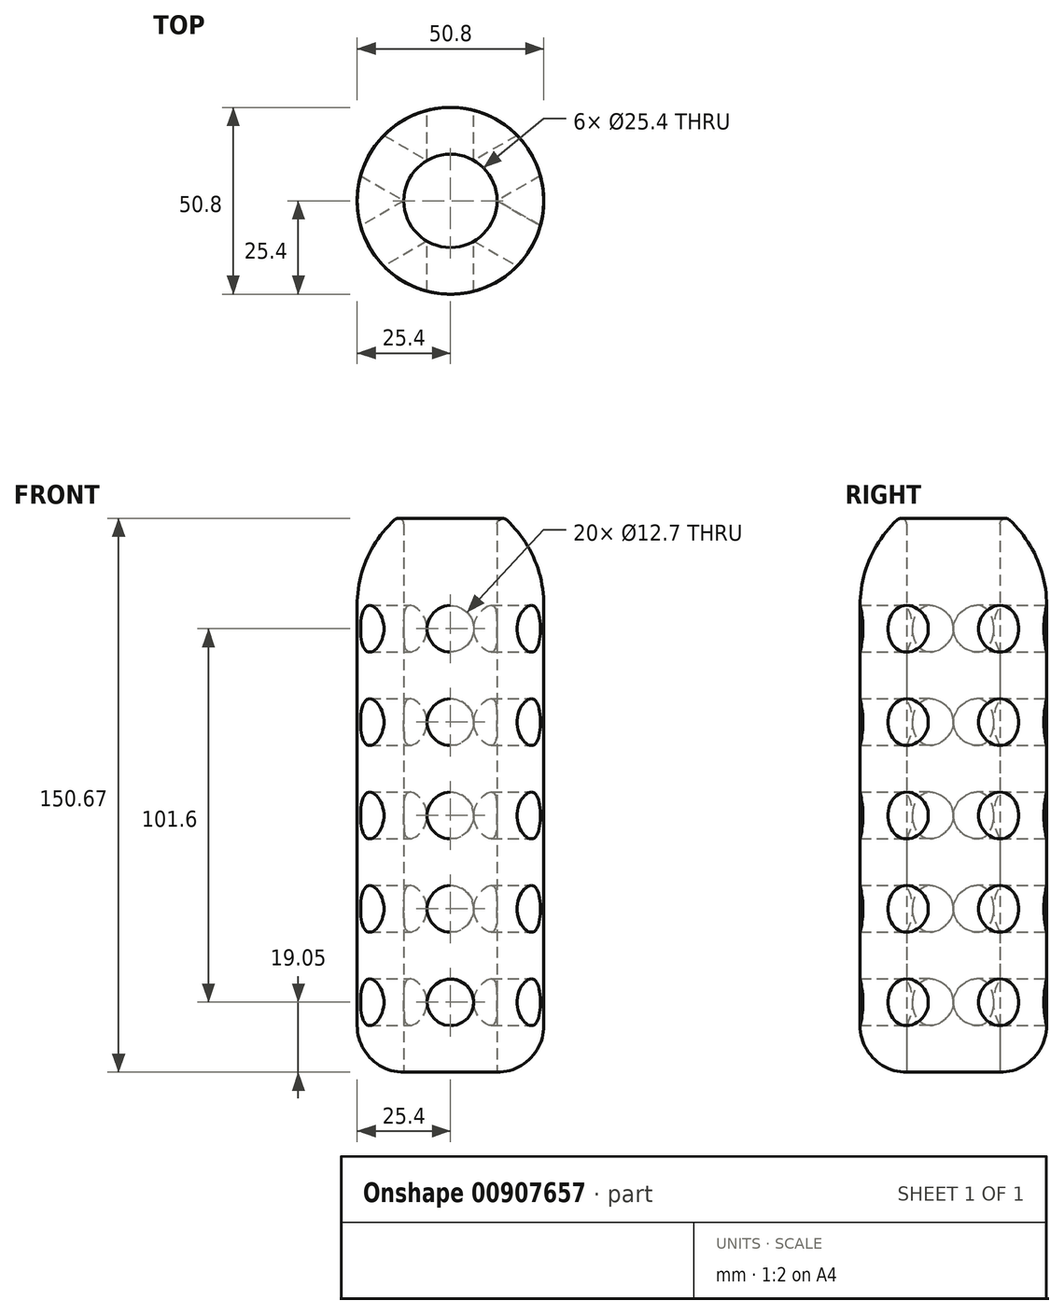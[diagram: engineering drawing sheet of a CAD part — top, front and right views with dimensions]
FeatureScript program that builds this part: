
annotation { "Feature Type Name" : "Feature", "Feature Type Description" : "" }
export const myFeature = defineFeature(function(context is Context, id is Id, definition is map)
    precondition{}
    {
        {
            var Q0;
            Q0=qCreatedBy(makeId("Front.planeOp"),FACE);
            var sketch = newSketch(context, id + "F0", { "sketchPlane" : qUnion([Q0])});
            skLineSegment(sketch, "E0", {"start": v(0, 0) * mm, "end": v(25.4, 0) * mm});
            skLineSegment(sketch, "E1", {"start": v(25.4, 0) * mm, "end": v(25.4, 127) * mm});
            skLineSegment(sketch, "E2", {"start": v(0, 0) * mm, "end": v(0, 152.4) * mm});
            skLineSegment(sketch, "E3", {"start": v(0, 152.4) * mm, "end": v(12.7, 152.4) * mm});
            skArc(sketch, "E4", {"start": v(25.4, 127) * mm, "mid": v(22.05, 141.2) * mm, "end": v(12.7, 152.4) * mm});
            skSolve(sketch);
        }
        {
            var Q0;
            Q0=makeQuery(id+"F0.imprint","IMPRINT",FACE,{"disambiguationData":[TD([[makeQuery(id+"F0.imprint","IMPRINT",EDGE,{"derivedFrom":sQuery(id+"F0.wireOp",EDGE,"E0")}),1.0]])]});
            var Q1;
            Q1=sQuery(id+"F0.wireOp",EDGE,"E2");
            revolve(context, id + "F1", {"surfaceOperationType" : NewSurfaceOperationType.NEW, "entities" : qUnion([Q0]), "axis" : qUnion([Q1]), "revolveType" : RevolveType.FULL});
        }
        {
            var Q0;
            Q0=qCreatedBy(makeId("Top.planeOp"),FACE);
            var sketch = newSketch(context, id + "F2", { "sketchPlane" : qUnion([Q0])});
            skCircle(sketch, "E5", {"center": v(0, 0) * mm, "radius": 12.7 * mm});
            skSolve(sketch);
        }
        {
            var Q0;
            Q0 = qSketchRegion(id + "F2", true);
            extrude(context, id + "F3", {"entities" : qUnion([Q0]), "operationType" : NewBodyOperationType.REMOVE, "depth" : 152.4 * mm, "offsetDistance" : 25.4 * mm});
        }
        {
            var Q0;
            Q0=makeQuery(id+"F3.boolean.opBoolean","MERGE",EDGE,{"derivedFrom":[makeQuery(id+"F1.opRevolve","SWEPT_EDGE",EDGE,{"disambiguationData":[OSD([sQuery(id+"F0.wireOp",EDGE,"E3"),sQuery(id+"F0.wireOp",EDGE,"E4")])]})],"fromTools":[makeQuery(id+"F3.opExtrude","CAP_EDGE",EDGE,{"disambiguationData":[OSD([sQuery(id+"F2.wireOp",EDGE,"E5")])],"isStart":false})]});
            fillet(context, id + "F4", {"entities" : qUnion([Q0]), "radius" : 1.52 * mm, "tangentPropagation" : true, "allowEdgeOverflow" : false});
        }
        {
            var Q0;
            Q0=makeQuery(id+"F1.opRevolve","SWEPT_EDGE",EDGE,{"disambiguationData":[OSD([sQuery(id+"F0.wireOp",EDGE,"E0"),sQuery(id+"F0.wireOp",EDGE,"E1")])]});
            fillet(context, id + "F5", {"entities" : qUnion([Q0]), "radius" : 12.7 * mm, "tangentPropagation" : true, "allowEdgeOverflow" : false});
        }
        {
            var Q0;
            Q0=qCreatedBy(makeId("Front.planeOp"),FACE);
            var sketch = newSketch(context, id + "F6", { "sketchPlane" : qUnion([Q0])});
            skCircle(sketch, "E6", {"center": v(0, 19.05) * mm, "radius": 6.35 * mm});
            skCircle(sketch, "E7", {"center": v(0, 44.45) * mm, "radius": 6.35 * mm});
            skCircle(sketch, "E8", {"center": v(0, 69.85) * mm, "radius": 6.35 * mm});
            skCircle(sketch, "E9", {"center": v(0, 95.25) * mm, "radius": 6.35 * mm});
            skCircle(sketch, "E10", {"center": v(0, 120.65) * mm, "radius": 6.35 * mm});
            skSolve(sketch);
        }
        {
            var Q0;
            Q0 = qSketchRegion(id + "F6", true);
            extrude(context, id + "F7", {"entities" : qUnion([Q0]), "operationType" : NewBodyOperationType.REMOVE, "endBound" : BoundingType.THROUGH_ALL, "oppositeDirection" : true, "depth" : 25.4 * mm, "offsetDistance" : 25.4 * mm, "hasSecondDirection" : true, "secondDirectionBound" : SecondDirectionBoundingType.THROUGH_ALL, "secondDirectionOppositeDirection" : false, "secondDirectionDepth" : 25.4 * mm});
        }
        {
            var Q0;
            Q0=qCreatedBy(makeId("Right.planeOp"),FACE);
            var sketch = newSketch(context, id + "F8", { "sketchPlane" : qUnion([Q0])});
            skLineSegment(sketch, "E11", {"start": v(0, 0) * mm, "end": v(0, 152.4) * mm});
            skSolve(sketch);
        }
        {
            var Q0;
            Q0=makeQuery(id+"F1.opRevolve","SWEPT_BODY",BODY,{"disambiguationData":[OSD([sQuery(id+"F0.wireOp",EDGE,"E0"),sQuery(id+"F0.wireOp",EDGE,"E1"),sQuery(id+"F0.wireOp",EDGE,"E2"),sQuery(id+"F0.wireOp",EDGE,"E3"),sQuery(id+"F0.wireOp",EDGE,"E4")])]});
            var Q1;
            Q1=sQuery(id+"F8.wireOp",EDGE,"E11");
            circularPattern(context, id + "F9", {"entities" : qUnion([Q0]), "axis" : qUnion([Q1]), "angle" : 360 * degree, "instanceCount" : 6, "equalSpace" : true});
        }
    });
